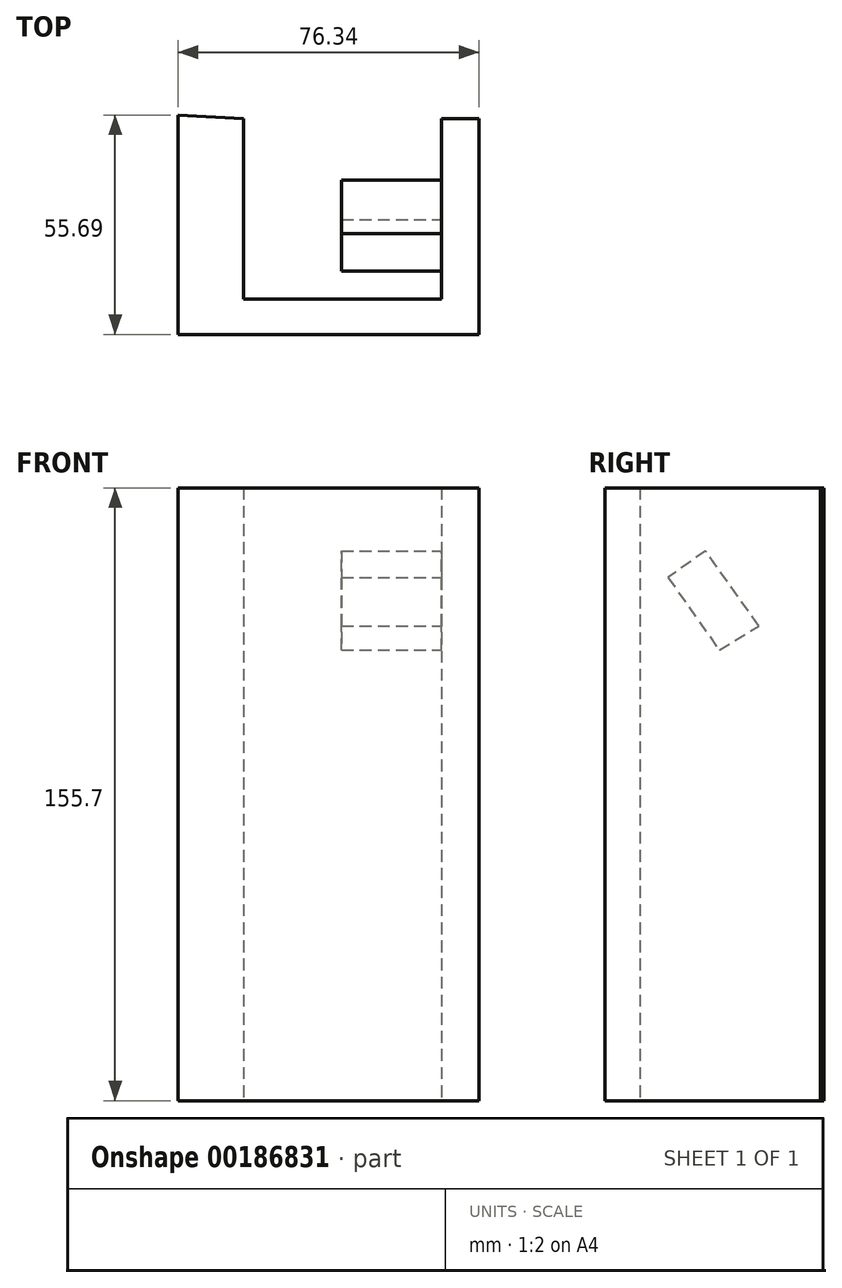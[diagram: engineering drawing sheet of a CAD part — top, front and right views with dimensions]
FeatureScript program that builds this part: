
annotation { "Feature Type Name" : "Feature", "Feature Type Description" : "" }
export const myFeature = defineFeature(function(context is Context, id is Id, definition is map)
    precondition{}
    {
        {
            var Q0;
            Q0=qCreatedBy(makeId("Top.planeOp"),FACE);
            var sketch = newSketch(context, id + "F0", { "sketchPlane" : qUnion([Q0])});
            skLineSegment(sketch, "E0", {"start": v(-51.64, 30.09) * mm, "end": v(-51.64, -25.6) * mm});
            skLineSegment(sketch, "E1", {"start": v(-51.64, -25.6) * mm, "end": v(24.7, -25.6) * mm});
            skLineSegment(sketch, "E2", {"start": v(24.7, -25.6) * mm, "end": v(24.7, 29.19) * mm});
            skLineSegment(sketch, "E3", {"start": v(24.7, 29.19) * mm, "end": v(15.27, 29.19) * mm});
            skLineSegment(sketch, "E4", {"start": v(15.27, 29.19) * mm, "end": v(15.27, -16.61) * mm});
            skLineSegment(sketch, "E5", {"start": v(15.27, -16.61) * mm, "end": v(-35.03, -16.61) * mm});
            skLineSegment(sketch, "E6", {"start": v(-35.03, -16.61) * mm, "end": v(-35.03, 29.19) * mm});
            skLineSegment(sketch, "E7", {"start": v(-35.03, 29.19) * mm, "end": v(-51.64, 30.09) * mm});
            skSolve(sketch);
        }
        {
            var Q0;
            Q0 = qSketchRegion(id + "F0", true);
            extrude(context, id + "F1", {"entities" : qUnion([Q0]), "depth" : 155.7 * mm});
        }
        {
            var Q0;
            Q0=makeQuery(id+"F1.opExtrude","SWEPT_FACE",FACE,{"disambiguationData":[OSD([sQuery(id+"F0.wireOp",EDGE,"E4")])]});
            var sketch = newSketch(context, id + "F2", { "sketchPlane" : qUnion([Q0])});
            skLineSegment(sketch, "E8", {"start": v(-13.54, 120.63) * mm, "end": v(0, 139.69) * mm});
            skLineSegment(sketch, "E9", {"start": v(0, 139.69) * mm, "end": v(9.55, 132.9) * mm});
            skLineSegment(sketch, "E10", {"start": v(9.55, 132.9) * mm, "end": v(-3.56, 114.44) * mm});
            skLineSegment(sketch, "E11", {"start": v(-3.56, 114.44) * mm, "end": v(-13.54, 120.63) * mm});
            skSolve(sketch);
        }
        {
            var Q0;
            Q0 = qSketchRegion(id + "F2", true);
            extrude(context, id + "F3", {"entities" : qUnion([Q0]), "operationType" : NewBodyOperationType.ADD, "depth" : 25.4 * mm});
        }
    });
